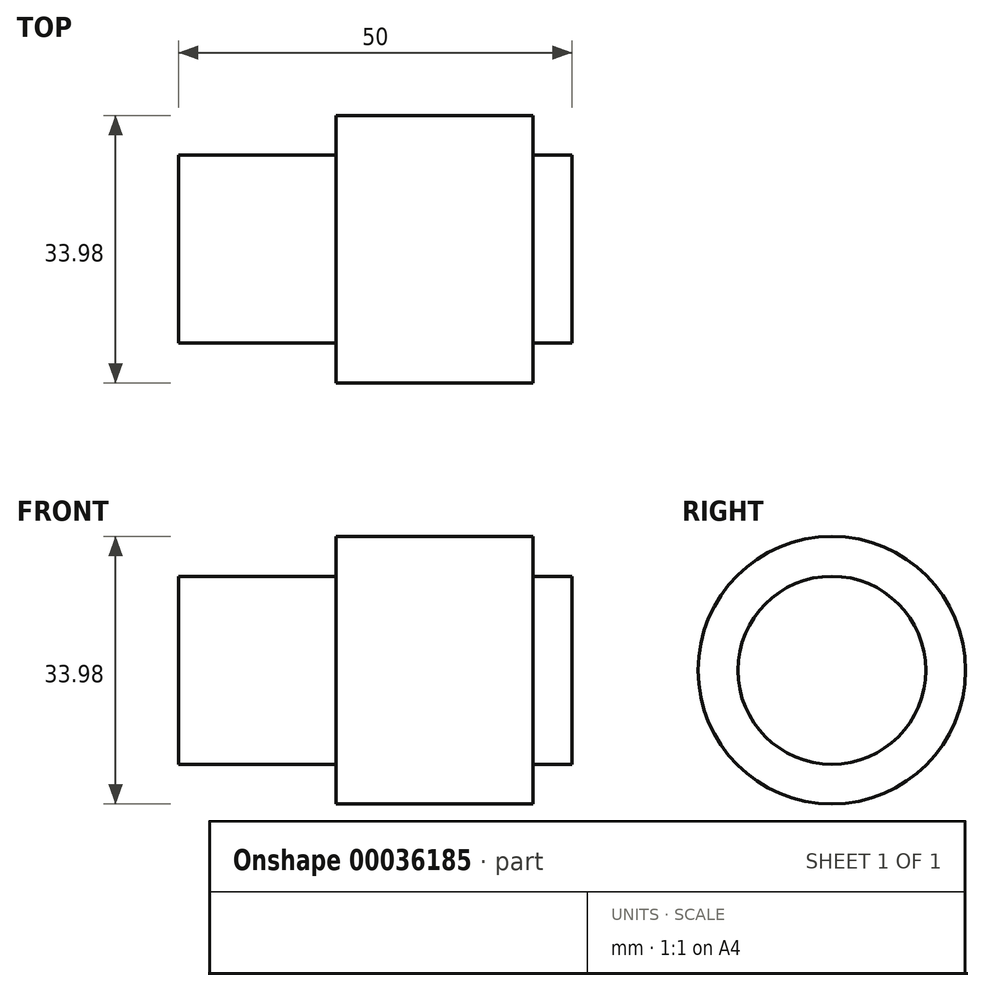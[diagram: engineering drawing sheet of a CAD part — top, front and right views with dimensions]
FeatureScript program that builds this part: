
annotation { "Feature Type Name" : "Feature", "Feature Type Description" : "" }
export const myFeature = defineFeature(function(context is Context, id is Id, definition is map)
    precondition{}
    {
        {
            var Q0;
            Q0=qCreatedBy(makeId("Front.planeOp"),FACE);
            var sketch = newSketch(context, id + "F0", { "sketchPlane" : qUnion([Q0])});
            skLineSegment(sketch, "E0", {"start": v(-23.17, 0) * mm, "end": v(26.83, 0) * mm});
            skLineSegment(sketch, "E1", {"start": v(26.83, 0) * mm, "end": v(26.83, 11.94) * mm});
            skLineSegment(sketch, "E2", {"start": v(26.83, 11.94) * mm, "end": v(21.83, 11.94) * mm});
            skLineSegment(sketch, "E3", {"start": v(21.83, 11.94) * mm, "end": v(21.83, 16.99) * mm});
            skLineSegment(sketch, "E4", {"start": v(21.83, 16.99) * mm, "end": v(-3.17, 16.99) * mm});
            skLineSegment(sketch, "E5", {"start": v(-3.17, 16.99) * mm, "end": v(-3.17, 11.94) * mm});
            skLineSegment(sketch, "E6", {"start": v(-3.17, 11.94) * mm, "end": v(-23.17, 11.94) * mm});
            skLineSegment(sketch, "E7", {"start": v(-23.17, 11.94) * mm, "end": v(-23.17, 0) * mm});
            skSolve(sketch);
        }
        {
            var Q0;
            Q0=makeQuery(id+"F0.imprint","IMPRINT",FACE,{"disambiguationData":[TD([[makeQuery(id+"F0.imprint","IMPRINT",EDGE,{"derivedFrom":sQuery(id+"F0.wireOp",EDGE,"E0")}),1.0]])]});
            var Q1;
            Q1=sQuery(id+"F0.wireOp",EDGE,"E0");
            revolve(context, id + "F1", {"entities" : qUnion([Q0]), "axis" : qUnion([Q1]), "revolveType" : RevolveType.FULL});
        }
    });
